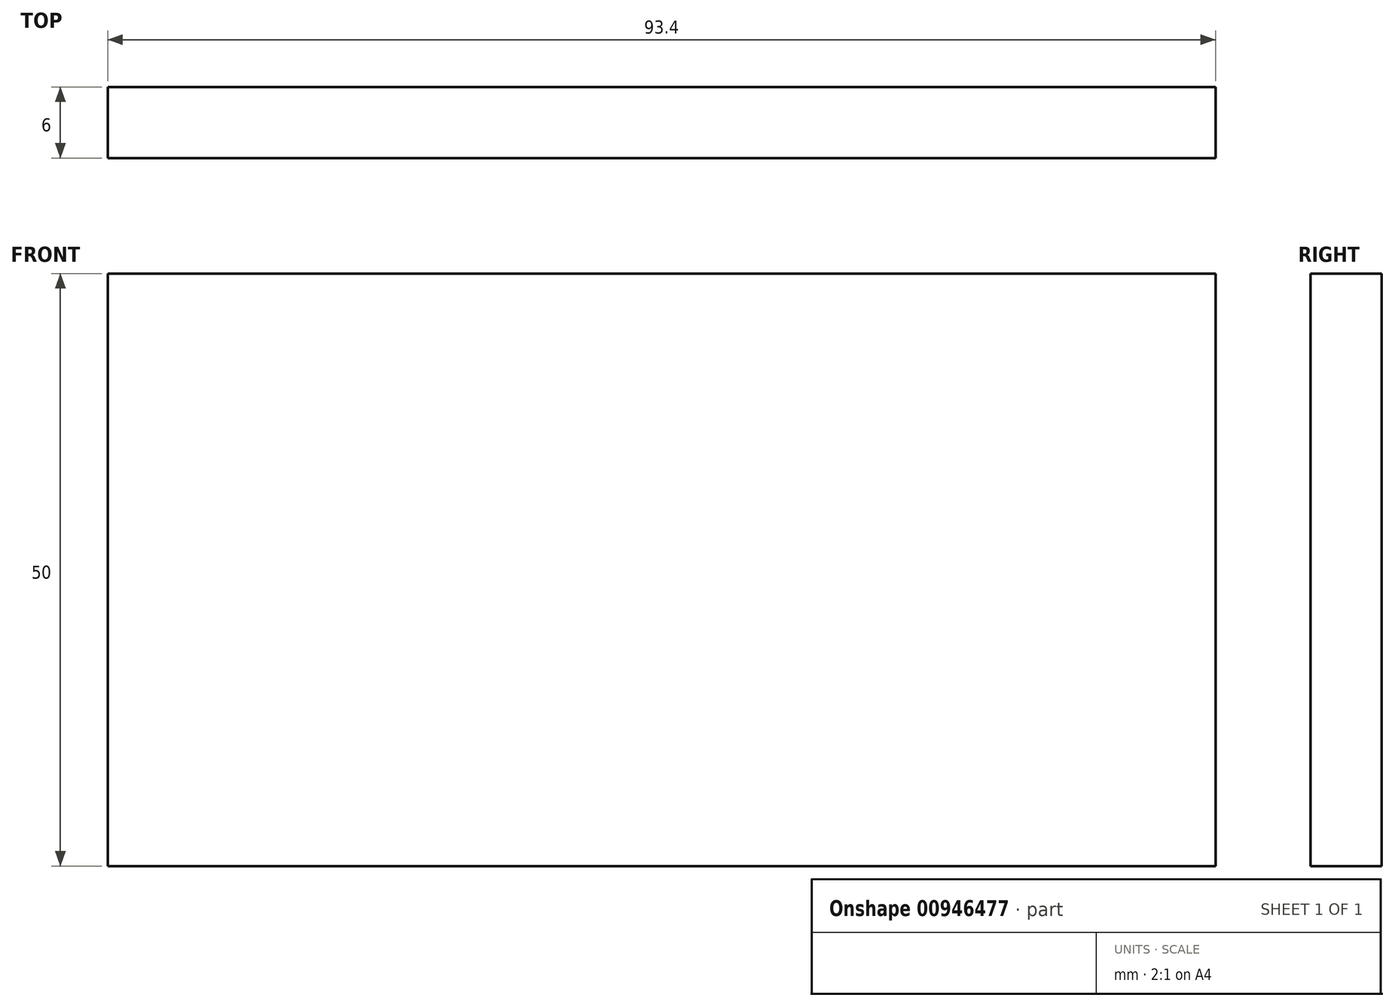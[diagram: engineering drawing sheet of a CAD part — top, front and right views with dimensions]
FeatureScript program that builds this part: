
annotation { "Feature Type Name" : "Feature", "Feature Type Description" : "" }
export const myFeature = defineFeature(function(context is Context, id is Id, definition is map)
    precondition{}
    {
        {
            var Q0;
            Q0=qCreatedBy(makeId("Front.planeOp"),FACE);
            var sketch = newSketch(context, id + "F0", { "sketchPlane" : qUnion([Q0])});
            skLineSegment(sketch, "E0.bottom", {"start": v(-46.7, 25) * mm, "end": v(46.7, 25) * mm});
            skLineSegment(sketch, "E0.top", {"start": v(-46.7, -25) * mm, "end": v(46.7, -25) * mm});
            skLineSegment(sketch, "E0.left", {"start": v(-46.7, 25) * mm, "end": v(-46.7, -25) * mm});
            skLineSegment(sketch, "E0.right", {"start": v(46.7, 25) * mm, "end": v(46.7, -25) * mm});
            skPoint(sketch, "E0.middle", {"position": v(0, 0) * mm});
            skSolve(sketch);
        }
        {
            var Q0;
            Q0=makeQuery(id+"F0.imprint","IMPRINT",FACE,{"disambiguationData":[TD([[makeQuery(id+"F0.imprint","IMPRINT",EDGE,{"derivedFrom":sQuery(id+"F0.wireOp",EDGE,"E0.bottom")}),-1.0]])]});
            extrude(context, id + "F1", {"entities" : qUnion([Q0]), "depth" : 6 * mm, "offsetDistance" : 25 * mm});
        }
    });
